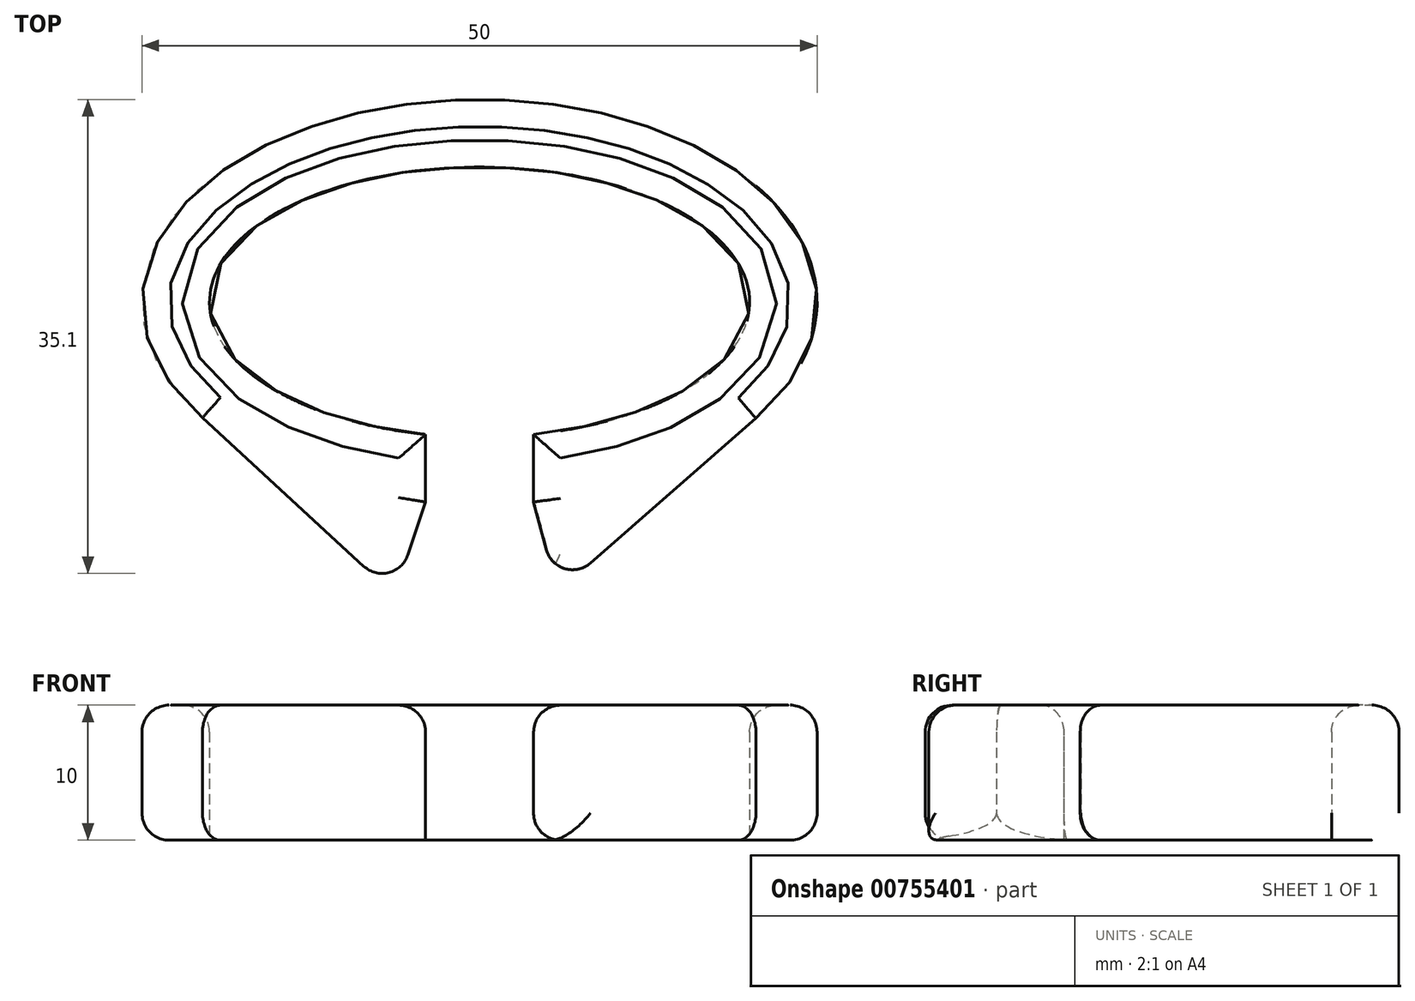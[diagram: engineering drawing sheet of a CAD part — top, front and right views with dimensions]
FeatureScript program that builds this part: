
annotation { "Feature Type Name" : "Feature", "Feature Type Description" : "" }
export const myFeature = defineFeature(function(context is Context, id is Id, definition is map)
    precondition{}
    {
        {
            var Q0;
            Q0=qCreatedBy(makeId("Top.planeOp"),FACE);
            var sketch = newSketch(context, id + "F0", { "sketchPlane" : qUnion([Q0])});
            skEllipse(sketch, "E0", {"center": v(0, 0) * mm, "majorRadius": 25 * mm, "minorRadius": 15 * mm, "majorAxis": v(1, 0)});
            skSolve(sketch);
        }
        {
            var Q0;
            Q0=makeQuery(id+"F0.imprint","IMPRINT",FACE,{"disambiguationData":[TD([[makeQuery(id+"F0.imprint","IMPRINT",EDGE,{"derivedFrom":sQuery(id+"F0.wireOp",EDGE,"E0")}),1.0]])]});
            extrude(context, id + "F1", {"entities" : qUnion([Q0]), "depth" : 10 * mm, "offsetDistance" : 25 * mm});
        }
        {
            var Q0;
            Q0=makeQuery(id+"F1.opExtrude","CAP_FACE",FACE,{"disambiguationData":[OSD([sQuery(id+"F0.wireOp",EDGE,"E0")])],"isStart":false});
            var sketch = newSketch(context, id + "F2", { "sketchPlane" : qUnion([Q0])});
            skEllipse(sketch, "E1", {"center": v(0, 0) * mm, "majorRadius": 20 * mm, "minorRadius": 10 * mm, "majorAxis": v(1, 0)});
            skSolve(sketch);
        }
        {
            var Q0;
            Q0=makeQuery(id+"F2.imprint","IMPRINT",FACE,{"disambiguationData":[TD([[makeQuery(id+"F2.imprint","IMPRINT",EDGE,{"derivedFrom":sQuery(id+"F2.wireOp",EDGE,"E1")}),1.0]])]});
            extrude(context, id + "F3", {"entities" : qUnion([Q0]), "operationType" : NewBodyOperationType.REMOVE, "oppositeDirection" : true, "depth" : 10 * mm, "offsetDistance" : 25 * mm});
        }
        {
            var Q0;
            Q0=makeQuery(id+"F1.opExtrude","CAP_FACE",FACE,{"disambiguationData":[OSD([sQuery(id+"F0.wireOp",EDGE,"E0")])],"isStart":false});
            var sketch = newSketch(context, id + "F4", { "sketchPlane" : qUnion([Q0])});
            skLineSegment(sketch, "E2.bottom", {"start": v(-4, -14.8) * mm, "end": v(4, -14.8) * mm});
            skLineSegment(sketch, "E2.top", {"start": v(-4, -5.2) * mm, "end": v(4, -5.2) * mm});
            skLineSegment(sketch, "E2.left", {"start": v(-4, -14.8) * mm, "end": v(-4, -5.2) * mm});
            skLineSegment(sketch, "E2.right", {"start": v(4, -14.8) * mm, "end": v(4, -5.2) * mm});
            skPoint(sketch, "E2.middle", {"position": v(0, -10) * mm});
            skSolve(sketch);
        }
        {
            var Q0;
            {var subQ0=sQuery(id+"F4.wireOp",EDGE,"E2.bottom");Q0=makeQuery(id+"F4.imprint","IMPRINT",FACE,{"disambiguationData":[TD([[makeQuery(id+"F4.imprint","IMPRINT",EDGE,{"derivedFrom":subQ0}),1.0]])]});}
            extrude(context, id + "F5", {"entities" : qUnion([Q0]), "operationType" : NewBodyOperationType.REMOVE, "oppositeDirection" : true, "depth" : 10 * mm, "offsetDistance" : 25 * mm});
        }
        {
            var Q0;
            {var subQ0=sQuery(id+"F0.wireOp",EDGE,"E0");Q0=makeQuery(id+"F5.boolean.opBoolean","SPLIT",FACE,{"disambiguationData":[TD([makeQuery(id+"F5.opExtrude","SWEPT_FACE",FACE,{"disambiguationData":[OSD([sQuery(id+"F4.wireOp",EDGE,"E2.bottom")])]})])],"derivedFrom":makeQuery(id+"F1.opExtrude","CAP_FACE",FACE,{"disambiguationData":[OSD([subQ0])],"isStart":false})});}
            extrude(context, id + "F6", {"entities" : qUnion([Q0]), "operationType" : NewBodyOperationType.REMOVE, "oppositeDirection" : true, "depth" : 10 * mm, "offsetDistance" : 25 * mm});
        }
        {
            var Q0;
            Q0=qCreatedBy(makeId("Top.planeOp"),FACE);
            var sketch = newSketch(context, id + "F7", { "sketchPlane" : qUnion([Q0])});
            skLineSegment(sketch, "E3", {"start": v(-4, -14.8) * mm, "end": v(-6.3, -21.66) * mm});
            skLineSegment(sketch, "E4", {"start": v(-6.3, -21.66) * mm, "end": v(-21.27, -7.88) * mm});
            skLineSegment(sketch, "E5", {"start": v(-21.27, -7.88) * mm, "end": v(-4, -14.8) * mm});
            skSolve(sketch);
        }
        {
            var Q0;
            Q0=makeQuery(id+"F7.imprint","IMPRINT",FACE,{"disambiguationData":[TD([[makeQuery(id+"F7.imprint","IMPRINT",EDGE,{"derivedFrom":sQuery(id+"F7.wireOp",EDGE,"E3")}),-1.0]])]});
            extrude(context, id + "F8", {"entities" : qUnion([Q0]), "operationType" : NewBodyOperationType.ADD, "depth" : 10 * mm, "offsetDistance" : 25 * mm});
        }
        {
            var Q0;
            Q0=qCreatedBy(makeId("Top.planeOp"),FACE);
            var sketch = newSketch(context, id + "F9", { "sketchPlane" : qUnion([Q0])});
            skLineSegment(sketch, "E6", {"start": v(4, -14.8) * mm, "end": v(5.79, -21.44) * mm});
            skLineSegment(sketch, "E7", {"start": v(5.79, -21.44) * mm, "end": v(20.47, -8.61) * mm});
            skLineSegment(sketch, "E8", {"start": v(20.47, -8.61) * mm, "end": v(4, -14.8) * mm});
            skSolve(sketch);
        }
        {
            var Q0;
            Q0=makeQuery(id+"F9.imprint","IMPRINT",FACE,{"disambiguationData":[TD([[makeQuery(id+"F9.imprint","IMPRINT",EDGE,{"derivedFrom":sQuery(id+"F9.wireOp",EDGE,"E6")}),1.0]])]});
            extrude(context, id + "F10", {"entities" : qUnion([Q0]), "operationType" : NewBodyOperationType.ADD, "depth" : 10 * mm, "offsetDistance" : 25 * mm});
        }
        {
            var Q0;
            Q0=makeQuery(id+"F3.boolean.opBoolean","COPY",EDGE,{"derivedFrom":makeQuery(id+"F3.opExtrude","CAP_EDGE",EDGE,{"disambiguationData":[OSD([sQuery(id+"F2.wireOp",EDGE,"E1")])],"isStart":false})});
            var Q1;
            {var subQ0=sQuery(id+"F0.wireOp",EDGE,"E0");Q1=makeQuery(id+"F10.boolean.opBoolean","MERGE",FACE,{"derivedFrom":[makeQuery(id+"F8.boolean.opBoolean","MERGE",FACE,{"derivedFrom":[makeQuery(id+"F5.boolean.opBoolean","SPLIT",FACE,{"disambiguationData":[TD([makeQuery(id+"F3.boolean.opBoolean","COPY",FACE,{"derivedFrom":makeQuery(id+"F3.opExtrude","SWEPT_FACE",FACE,{"disambiguationData":[OSD([sQuery(id+"F2.wireOp",EDGE,"E1")])]})})])],"derivedFrom":makeQuery(id+"F1.opExtrude","CAP_FACE",FACE,{"disambiguationData":[OSD([subQ0])],"isStart":false})}),makeQuery(id+"F8.opExtrude","CAP_FACE",FACE,{"disambiguationData":[OSD([sQuery(id+"F7.wireOp",EDGE,"E3"),sQuery(id+"F7.wireOp",EDGE,"E4"),sQuery(id+"F7.wireOp",EDGE,"E5")])],"isStart":false})]}),makeQuery(id+"F10.opExtrude","CAP_FACE",FACE,{"disambiguationData":[OSD([sQuery(id+"F9.wireOp",EDGE,"E6"),sQuery(id+"F9.wireOp",EDGE,"E7"),sQuery(id+"F9.wireOp",EDGE,"E8")])],"isStart":false})]});}
            var Q2;
            Q2=makeQuery(id+"F8.opExtrude","SWEPT_EDGE",EDGE,{"disambiguationData":[OSD([sQuery(id+"F7.wireOp",EDGE,"E3"),sQuery(id+"F7.wireOp",EDGE,"E4")])]});
            var Q3;
            Q3=makeQuery(id+"F10.opExtrude","SWEPT_EDGE",EDGE,{"disambiguationData":[OSD([sQuery(id+"F9.wireOp",EDGE,"E6"),sQuery(id+"F9.wireOp",EDGE,"E7")])]});
            var Q4;
            Q4=makeQuery(id+"F5.boolean.opBoolean","COPY",EDGE,{"derivedFrom":makeQuery(id+"F5.opExtrude","SWEPT_EDGE",EDGE,{"disambiguationData":[OSD([sQuery(id+"F2.wireOp",EDGE,"E1"),sQuery(id+"F4.wireOp",EDGE,"E2.right")])]})});
            var Q5;
            Q5=makeQuery(id+"F5.boolean.opBoolean","COPY",EDGE,{"derivedFrom":makeQuery(id+"F5.opExtrude","SWEPT_EDGE",EDGE,{"disambiguationData":[OSD([sQuery(id+"F2.wireOp",EDGE,"E1"),sQuery(id+"F4.wireOp",EDGE,"E2.left")])]})});
            var Q6;
            {var subQ0=sQuery(id+"F7.wireOp",EDGE,"E4");var subQ1=sQuery(id+"F0.wireOp",EDGE,"E0");Q6=makeQuery(id+"F10.boolean.opBoolean","SPLIT",EDGE,{"disambiguationData":[TD([makeQuery(id+"F8.opExtrude","SWEPT_FACE",FACE,{"disambiguationData":[OSD([subQ0])]})])],"derivedFrom":makeQuery(id+"F5.boolean.opBoolean","SPLIT",EDGE,{"disambiguationData":[TD([makeQuery(id+"F5.opExtrude","SWEPT_FACE",FACE,{"disambiguationData":[OSD([sQuery(id+"F4.wireOp",EDGE,"E2.left")])]})])],"derivedFrom":makeQuery(id+"F1.opExtrude","CAP_EDGE",EDGE,{"disambiguationData":[OSD([subQ1])],"isStart":true})})});}
            var Q7;
            Q7=makeQuery(id+"F8.opExtrude","CAP_EDGE",EDGE,{"disambiguationData":[OSD([sQuery(id+"F7.wireOp",EDGE,"E3")])],"isStart":true});
            var Q8;
            Q8=makeQuery(id+"F5.boolean.opBoolean","COPY",EDGE,{"derivedFrom":makeQuery(id+"F5.opExtrude","CAP_EDGE",EDGE,{"disambiguationData":[OSD([sQuery(id+"F4.wireOp",EDGE,"E2.right")])],"isStart":false})});
            fillet(context, id + "F11", {"entities" : qUnion([Q0, Q1, Q2, Q3, Q4, Q5, Q6, Q7, Q8]), "radius" : 2 * mm, "tangentPropagation" : true, "allowEdgeOverflow" : false});
        }
    });
